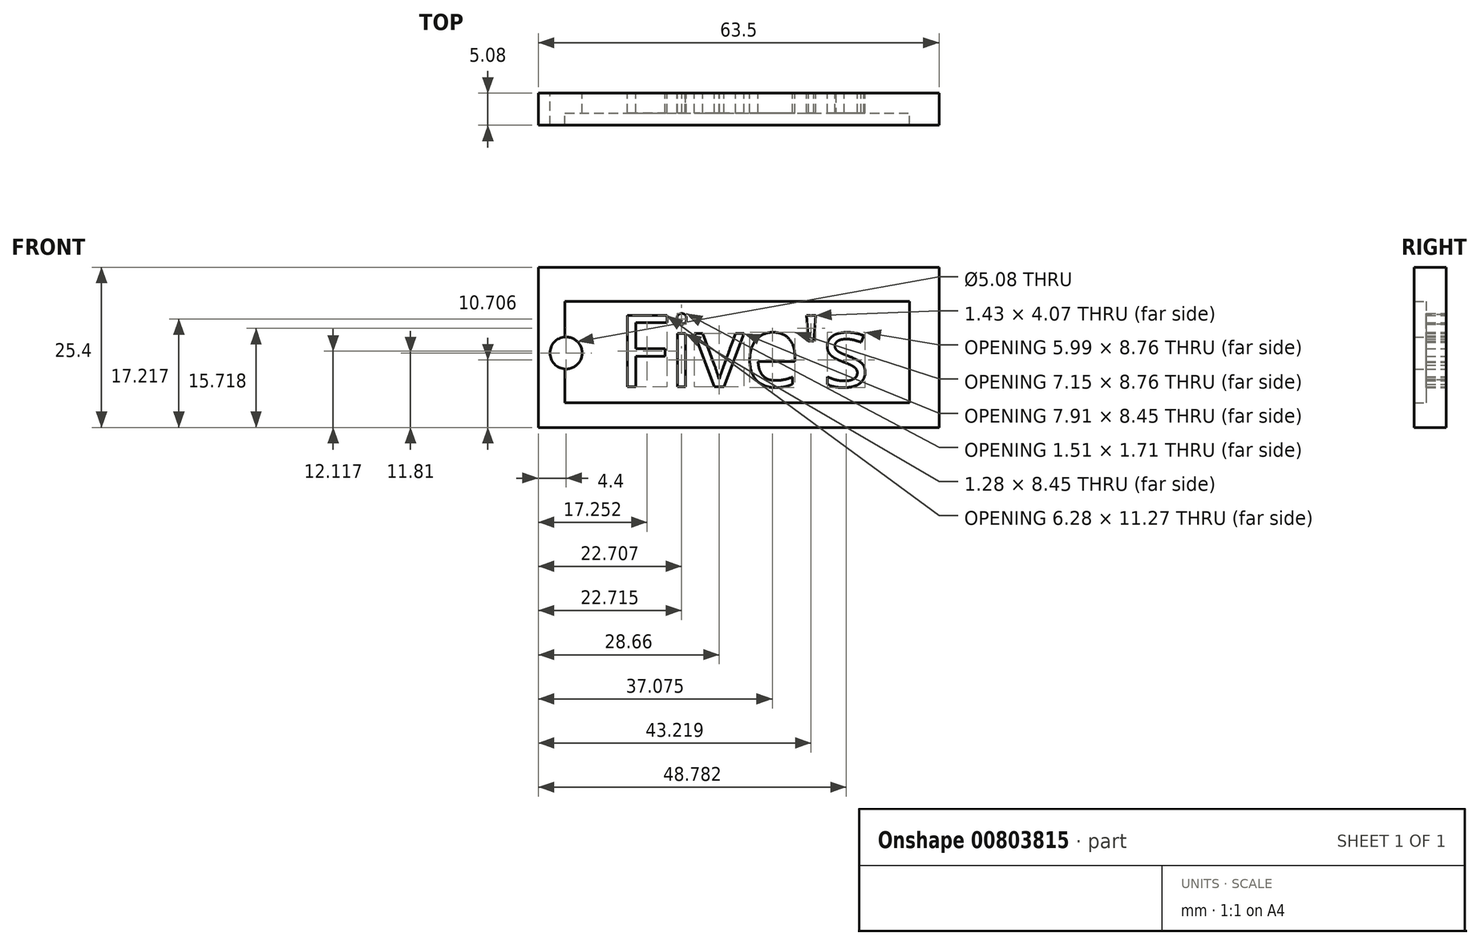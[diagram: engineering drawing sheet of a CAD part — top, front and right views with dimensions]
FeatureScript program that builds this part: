
annotation { "Feature Type Name" : "Feature", "Feature Type Description" : "" }
export const myFeature = defineFeature(function(context is Context, id is Id, definition is map)
    precondition{}
    {
        {
            var Q0;
            Q0=qCreatedBy(makeId("Front.planeOp"),FACE);
            var sketch = newSketch(context, id + "F0", { "sketchPlane" : qUnion([Q0])});
            skLineSegment(sketch, "E0", {"start": v(0, 0) * mm, "end": v(0, 25.4) * mm});
            skLineSegment(sketch, "E1", {"start": v(0, 25.4) * mm, "end": v(63.5, 25.4) * mm});
            skLineSegment(sketch, "E2", {"start": v(63.5, 25.4) * mm, "end": v(63.5, 0) * mm});
            skLineSegment(sketch, "E3", {"start": v(63.5, 0) * mm, "end": v(0, 0) * mm});
            skLineSegment(sketch, "E4.bottom", {"start": v(4.23, 20) * mm, "end": v(58.84, 20) * mm});
            skLineSegment(sketch, "E4.top", {"start": v(4.23, 3.94) * mm, "end": v(58.84, 3.94) * mm});
            skLineSegment(sketch, "E4.left", {"start": v(4.23, 20) * mm, "end": v(4.23, 3.94) * mm});
            skLineSegment(sketch, "E4.right", {"start": v(58.84, 20) * mm, "end": v(58.84, 3.94) * mm});
            skText(sketch, "E5", { "text": "Five\'s", "fontName": "OpenSans-Regular.ttf"});
            const initialGuessF0  = {"E5": [0.01256, 0.00648, 1, 0, 0.01137]};
            skSetInitialGuess(sketch, initialGuessF0);
            skSolve(sketch);
        }
        {
            var Q0;
            Q0 = qSketchRegion(id + "F0", true);
            extrude(context, id + "F1", {"entities" : qUnion([Q0]), "depth" : 5.08 * mm, "offsetDistance" : 25.4 * mm});
        }
        {
            var Q0;
            Q0=makeQuery(id+"F0.imprint","IMPRINT",FACE,{"disambiguationData":[TD([[makeQuery(id+"F0.imprint","IMPRINT",EDGE,{"derivedFrom":sQuery(id+"F0.wireOp",EDGE,"E4.bottom")}),-1.0]])]});
            extrude(context, id + "F2", {"entities" : qUnion([Q0]), "operationType" : NewBodyOperationType.ADD, "depth" : 3.17 * mm, "offsetDistance" : 25.4 * mm});
        }
        {
            var Q0;
            Q0=qCreatedBy(makeId("Front.planeOp"),FACE);
            var sketch = newSketch(context, id + "F3", { "sketchPlane" : qUnion([Q0])});
            skCircle(sketch, "E6", {"center": v(4.4, 11.8) * mm, "radius": 2.54 * mm});
            skSolve(sketch);
        }
        {
            var Q0;
            Q0 = qSketchRegion(id + "F3", true);
            extrude(context, id + "F4", {"entities" : qUnion([Q0]), "operationType" : NewBodyOperationType.REMOVE, "depth" : 25.4 * mm, "offsetDistance" : 25.4 * mm});
        }
        {
            var Q0;
            Q0=makeQuery(id+"F2.opExtrude","CAP_FACE",FACE,{"disambiguationData":[OSD([sQuery(id+"F0.wireOp",EDGE,"E4.bottom"),sQuery(id+"F0.wireOp",EDGE,"E4.top"),sQuery(id+"F0.wireOp",EDGE,"E4.left"),sQuery(id+"F0.wireOp",EDGE,"E4.right"),sQuery(id+"F0.wireOp",EDGE,"E5.sketch_text.stroke-0"),sQuery(id+"F0.wireOp",EDGE,"E5.sketch_text.stroke-1"),sQuery(id+"F0.wireOp",EDGE,"E5.sketch_text.stroke-2"),sQuery(id+"F0.wireOp",EDGE,"E5.sketch_text.stroke-3"),sQuery(id+"F0.wireOp",EDGE,"E5.sketch_text.stroke-4"),sQuery(id+"F0.wireOp",EDGE,"E5.sketch_text.stroke-5"),sQuery(id+"F0.wireOp",EDGE,"E5.sketch_text.stroke-6"),sQuery(id+"F0.wireOp",EDGE,"E5.sketch_text.stroke-7"),sQuery(id+"F0.wireOp",EDGE,"E5.sketch_text.stroke-8"),sQuery(id+"F0.wireOp",EDGE,"E5.sketch_text.stroke-9"),sQuery(id+"F0.wireOp",EDGE,"E5.sketch_text.stroke-10"),sQuery(id+"F0.wireOp",EDGE,"E5.sketch_text.stroke-11"),sQuery(id+"F0.wireOp",EDGE,"E5.sketch_text.stroke-12"),sQuery(id+"F0.wireOp",EDGE,"E5.sketch_text.stroke-13"),sQuery(id+"F0.wireOp",EDGE,"E5.sketch_text.stroke-14"),sQuery(id+"F0.wireOp",EDGE,"E5.sketch_text.stroke-15"),sQuery(id+"F0.wireOp",EDGE,"E5.sketch_text.stroke-16"),sQuery(id+"F0.wireOp",EDGE,"E5.sketch_text.stroke-17"),sQuery(id+"F0.wireOp",EDGE,"E5.sketch_text.stroke-18"),sQuery(id+"F0.wireOp",EDGE,"E5.sketch_text.stroke-19"),sQuery(id+"F0.wireOp",EDGE,"E5.sketch_text.stroke-20"),sQuery(id+"F0.wireOp",EDGE,"E5.sketch_text.stroke-21"),sQuery(id+"F0.wireOp",EDGE,"E5.sketch_text.stroke-22"),sQuery(id+"F0.wireOp",EDGE,"E5.sketch_text.stroke-23"),sQuery(id+"F0.wireOp",EDGE,"E5.sketch_text.stroke-24"),sQuery(id+"F0.wireOp",EDGE,"E5.sketch_text.stroke-25"),sQuery(id+"F0.wireOp",EDGE,"E5.sketch_text.stroke-26"),sQuery(id+"F0.wireOp",EDGE,"E5.sketch_text.stroke-27"),sQuery(id+"F0.wireOp",EDGE,"E5.sketch_text.stroke-28"),sQuery(id+"F0.wireOp",EDGE,"E5.sketch_text.stroke-29"),sQuery(id+"F0.wireOp",EDGE,"E5.sketch_text.stroke-30"),sQuery(id+"F0.wireOp",EDGE,"E5.sketch_text.stroke-31"),sQuery(id+"F0.wireOp",EDGE,"E5.sketch_text.stroke-32"),sQuery(id+"F0.wireOp",EDGE,"E5.sketch_text.stroke-33"),sQuery(id+"F0.wireOp",EDGE,"E5.sketch_text.stroke-34"),sQuery(id+"F0.wireOp",EDGE,"E5.sketch_text.stroke-35"),sQuery(id+"F0.wireOp",EDGE,"E5.sketch_text.stroke-36"),sQuery(id+"F0.wireOp",EDGE,"E5.sketch_text.stroke-37"),sQuery(id+"F0.wireOp",EDGE,"E5.sketch_text.stroke-38"),sQuery(id+"F0.wireOp",EDGE,"E5.sketch_text.stroke-39"),sQuery(id+"F0.wireOp",EDGE,"E5.sketch_text.stroke-40"),sQuery(id+"F0.wireOp",EDGE,"E5.sketch_text.stroke-41"),sQuery(id+"F0.wireOp",EDGE,"E5.sketch_text.stroke-42"),sQuery(id+"F0.wireOp",EDGE,"E5.sketch_text.stroke-43"),sQuery(id+"F0.wireOp",EDGE,"E5.sketch_text.stroke-44"),sQuery(id+"F0.wireOp",EDGE,"E5.sketch_text.stroke-45"),sQuery(id+"F0.wireOp",EDGE,"E5.sketch_text.stroke-51"),sQuery(id+"F0.wireOp",EDGE,"E5.sketch_text.stroke-52"),sQuery(id+"F0.wireOp",EDGE,"E5.sketch_text.stroke-53"),sQuery(id+"F0.wireOp",EDGE,"E5.sketch_text.stroke-54"),sQuery(id+"F0.wireOp",EDGE,"E5.sketch_text.stroke-55"),sQuery(id+"F0.wireOp",EDGE,"E5.sketch_text.stroke-56"),sQuery(id+"F0.wireOp",EDGE,"E5.sketch_text.stroke-57"),sQuery(id+"F0.wireOp",EDGE,"E5.sketch_text.stroke-58"),sQuery(id+"F0.wireOp",EDGE,"E5.sketch_text.stroke-59"),sQuery(id+"F0.wireOp",EDGE,"E5.sketch_text.stroke-60"),sQuery(id+"F0.wireOp",EDGE,"E5.sketch_text.stroke-61"),sQuery(id+"F0.wireOp",EDGE,"E5.sketch_text.stroke-62"),sQuery(id+"F0.wireOp",EDGE,"E5.sketch_text.stroke-63"),sQuery(id+"F0.wireOp",EDGE,"E5.sketch_text.stroke-64"),sQuery(id+"F0.wireOp",EDGE,"E5.sketch_text.stroke-65"),sQuery(id+"F0.wireOp",EDGE,"E5.sketch_text.stroke-66"),sQuery(id+"F0.wireOp",EDGE,"E5.sketch_text.stroke-67"),sQuery(id+"F0.wireOp",EDGE,"E5.sketch_text.stroke-68"),sQuery(id+"F0.wireOp",EDGE,"E5.sketch_text.stroke-69"),sQuery(id+"F0.wireOp",EDGE,"E5.sketch_text.stroke-70"),sQuery(id+"F0.wireOp",EDGE,"E5.sketch_text.stroke-71"),sQuery(id+"F0.wireOp",EDGE,"E5.sketch_text.stroke-72"),sQuery(id+"F0.wireOp",EDGE,"E5.sketch_text.stroke-73"),sQuery(id+"F0.wireOp",EDGE,"E5.sketch_text.stroke-74"),sQuery(id+"F0.wireOp",EDGE,"E5.sketch_text.stroke-75"),sQuery(id+"F0.wireOp",EDGE,"E5.sketch_text.stroke-76"),sQuery(id+"F0.wireOp",EDGE,"E5.sketch_text.stroke-77"),sQuery(id+"F0.wireOp",EDGE,"E5.sketch_text.stroke-78"),sQuery(id+"F0.wireOp",EDGE,"E5.sketch_text.stroke-79")])],"isStart":false});
            extrude(context, id + "F5", {"entities" : qUnion([Q0]), "operationType" : NewBodyOperationType.ADD, "surfaceOperationType" : NewSurfaceOperationType.ADD, "oppositeDirection" : true, "depth" : 3.17 * mm, "offsetDistance" : 25.4 * mm});
        }
    });
